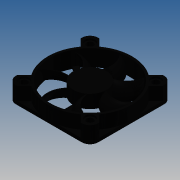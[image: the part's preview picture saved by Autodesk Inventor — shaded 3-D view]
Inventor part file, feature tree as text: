
AUTODESK INVENTOR PART (.ipt)
format: ipt  version: 2015 (Build 190159000, 159)  size: 460,288 bytes
history: native  units: mm
features: sketch x13, extrude x9, projected_geometry x6, pattern_circular x4, plane x4, loft x1
ambient origin geometry x8: Origin, YZ Plane, XZ Plane, XY Plane, X Axis, Y Axis, Z Axis, Center Point
bodies: Solid1 (feature_tree)
feature tree (37):
  extrude  "Extrusion1"  Depth=50.0mm
  extrude  "Extrusion2"  Depth=40.0mm
  extrude  "Extrusion3"  Depth=4.0mm
  extrude  "Extrusion5"  Depth=4.0mm
  extrude  "Extrusion6"  Depth=2.0mm TaperAngle=0.0deg
  pattern_circular  "Circular Pattern2"  Count=3 Angle=360.0deg
  extrude  "Extrusion7"  Depth=1.0mm
  plane  "Work Plane2"
  sketch  "Sketch9"  dims[d12=8.0mm d13=0.0mm]
  sketch  "Sketch10"  dims[d14=8.0mm d15=0.0mm]
  plane  "Work Plane3"
  sketch  "Sketch11"  dims[d23=12.0mm]
  plane  "Work Plane4"
  loft  "Loft1"
  extrude  "Extrusion9"  Depth=1.0mm
  pattern_circular  "Circular Pattern4"  [2 undecoded]
  extrude  "Extrusion10"  Depth=1.0mm
  pattern_circular  "Circular Pattern5"  [2 undecoded]
  extrude  "Extrusion11"  Depth=1.0mm
  pattern_circular  "Circular Pattern6"  Angle=90.0deg  [1 undecoded]
  sketch  "Sketch1"  dims[d0=50.0mm d1=50.0mm]
  sketch  "Sketch2"  dims[d2=40.0mm d3=40.0mm]
  sketch  "Sketch3"  dims[d4=4.0mm d5=4.0mm]
  projected_geometry  "Projected Loop1"
  sketch  "Sketch5"  dims[d6=4.0mm d7=4.0mm]
  sketch  "Sketch6"  dims[d8=5.0mm d9=2.0mm d10=0.0mm]
  projected_geometry  "Projected Loop3"
  projected_geometry  "Projected Loop4"
  sketch  "Sketch7"  dims[d11=1.5mm]
  plane  "Work Plane1"
  sketch  "Sketch12"  dims[d24=2.0mm d25=0.0mm]
  sketch  "Sketch13"  dims[d26=1.5mm]
  projected_geometry  "Projected Loop5"
  sketch  "Sketch14"  dims[d27=1.5mm]
  projected_geometry  "Projected Loop6"
  sketch  "Sketch15"  dims[d28=1.2mm d29=0.0mm d30=30.0mm d31=360.0deg d33=20.0mm d34=8.0mm d35=0.0mm d42=13.0mm d43=1.8mm d44=2.2mm d45=5.0mm d46=1.0mm d47=0.0mm d48=90.0deg d49=0.0mm d50=90.0deg d51=0.0mm d52=90.0deg d53=0.0mm d54=90.0deg d55=1.0mm d56=0.0mm d57=70.0mm d58=360.0deg d60=4.0mm d61=4.0mm d62=4.0mm d63=8.0mm d64=0.0mm d65=40.0mm d66=360.0deg d68=1.0mm d69=1.0mm d70=0.0mm d71=40.0mm d72=360.0deg]
  projected_geometry  "Projected Loop7"
note: 5 required parameter values undecoded (feature->parameter linkage not recoverable at this tier; creation-order binding heuristic only, values carry confidence <= 0.55)
